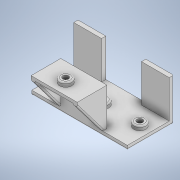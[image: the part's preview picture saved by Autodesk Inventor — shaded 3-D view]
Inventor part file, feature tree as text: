
AUTODESK INVENTOR PART (.ipt)
format: ipt  version: 2020 (Build 240168000, 168)  size: 324,608 bytes
history: native  units: in
note: dims shown in document units (in); Inventor stores cm internally (conversion verified against a paired STEP export)
features: extrude x17, sketch x17, fillet x3
ambient origin geometry x8: Origin, YZ Plane, XZ Plane, XY Plane, X Axis, Y Axis, Z Axis, Center Point
bodies: Solid1 (feature_tree)
feature tree (37):
  extrude  "Extrusion1"  Depth=1.2756in
  extrude  "Extrusion3"  Depth=0.1181in
  extrude  "Extrusion4"  Depth=1.0394in TaperAngle=0.0deg
  extrude  "Extrusion5"  Depth=0.1181in TaperAngle=0.0deg
  extrude  "Extrusion6"  Depth=0.1181in TaperAngle=0.0deg
  extrude  "Extrusion9"  Depth=0.3346in
  extrude  "Extrusion10"  Depth=1.0236in
  extrude  "Extrusion11"  Depth=0.2953in
  extrude  "Extrusion14"  Depth=0.3346in
  fillet  "Fillet1"  Radius=0.1181in
  extrude  "Extrusion15"  Depth=0.1181in
  extrude  "Extrusion16"  Depth=0.1772in TaperAngle=0.0deg
  extrude  "Extrusion17"  Depth=0.0394in
  extrude  "Extrusion18"  Depth=0.1575in
  extrude  "Extrusion19"  Depth=0.3937in
  extrude  "Extrusion20"  Depth=0.2362in
  extrude  "Extrusion21"  Depth=1.2756in
  extrude  "Extrusion22"  Depth=0.0394in
  fillet  "Fillet3"  Radius=0.7018in
  fillet  "Fillet4"  Radius=0.1181in
  sketch  "Sketch1"  dims[d0=1.6142in d1=1.2756in]
  sketch  "Sketch3"  dims[d2=0.1181in d3=0.0in d8=0.1181in]
  sketch  "Sketch4"  dims[d9=0.1181in d10=1.0394in d11=0.0in]
  sketch  "Sketch5"  dims[d12=0.8465in d13=0.1181in d14=0.0in]
  sketch  "Sketch6"  dims[d15=0.8465in d16=0.1181in d17=0.0in]
  sketch  "Sketch9"  dims[d20=0.3346in d21=0.3346in]
  sketch  "Sketch10"  dims[d22=0.1181in d23=0.0in d32=1.0236in]
  sketch  "Sketch11"  dims[d33=0.2953in d34=0.2953in]
  sketch  "Sketch14"  dims[d35=1.0236in d36=0.0in d37=0.3346in d38=0.1181in d39=0.0in]
  sketch  "Sketch15"  dims[d40=0.7677in d41=0.1181in]
  sketch  "Sketch16"  dims[d42=1.0394in d43=0.0in d50=0.1772in d51=0.0in]
  sketch  "Sketch17"  dims[d52=0.0394in d54=0.1575in]
  sketch  "Sketch18"  dims[d55=0.1575in d56=0.1575in]
  sketch  "Sketch19"  dims[d57=0.3937in d58=0.0in d59=0.2362in]
  sketch  "Sketch20"  dims[d60=0.2362in d61=0.2362in]
  sketch  "Sketch21"  dims[d62=0.1181in d63=0.0in d64=1.2756in]
  sketch  "Sketch22"  dims[d65=0.1181in d66=0.1181in d67=0.7018in d68=0.1181in d69=1.0394in d70=0.0in d71=0.1181in d72=0.7018in d73=0.0in d74=1.0394in d75=1.2756in d76=0.0in d77=0.1575in d78=1.2756in d79=0.0in d80=0.3346in d81=0.1181in d82=0.0in d83=0.2362in d84=0.1181in d85=0.0in d86=0.0394in d87=0.0394in d44=0.0197in d45=0.0344in]
